# Revit family: Building-ConnessioniIEC309-GEWISS-67IB-PRESE-INTERBLOCCATE_IP67_SENZA_FONDO_FUS
name_source: partatom
category: Apparecchi elettrici
units: mm (PartAtom-declared; Revit-internal decimal feet)

## family parameters
Condiviso = Sì
Host = Superficie
Mantenere orientamento annotazione = Sì
Punto di calcolo locali = Sì
Quota connettore circolare = Usa diametro
Taglio con vuoti quando caricato = Sì
Tipo di parte = Normale

## types (23) — shared parameters
Catalogo = BUILDING
Catalogo Serie = 67 IB
Codice Electrocod = 2222
Con fondo = No
Corpo presa = GEWISS -BLU
Corrente nominale di cortocircuito (Icc) = 10KA
Frequenza = 50/60 Hz
Frequenza nominale (Hz) = 50/60 Hz
Glow Wire Test = 850 °C
Glow wire test: = 850 °C
Grado di protezione = IP67
IDF = 249aa0f0-cb6e-4699-9a5f-455441d8fc5e
IDT = 5410a18b-86cc-47a6-890a-93cf755ebe5d
Immagine tipo = G.jpg
Potere di interruzione fusibili = > 50 kA
Produttore = GEWISS S.p.A.
Prospetto di default = 1219 mm
Protezione = Base portafusibile (CBF)
Resistenza agli urti = IK08
SEO = Presa
Scheda Tecnica = https://www.gewiss.com
Simbolo presa = PRESAINDSTAGNA : 3P
Struttura = Grigio RAL - 7035
Temperatura di funzionamento = -25 ÷ +40 °C
Temperatura di utilizzo = -25 +40 °C
Tensione nominale di isolamento (Ui) = 500V
Tensione nominale di tenuta ad impulso = 4KV
Termopressione con biglia = 125 °C
Tipo fusibile = Ã˜ 10,3x38 mm
Tipologia = Verticale
URL = https://www.gewiss.com
Versione file RFA = 21.4
presa = rosso
zero-valued in all types: giallo

## per-type parameters (varying)
| type | Codice EAN | Colore | Colore: | Corrente nominale (A) | Corrente nominale (In) | Corrente nominale (In) presa IB | Descrizione | Modello | N. poli | Numero di poli | Peso | Peso (kg) | Riferimento h | Tensione nominale | Tensione nominale: |
| GW66323N - PR.BL IP67 S.F.2P+T 16A 110V 4H CBF | 8011564741782 | Giallo | Giallo | 16 | 16 | 16A | PR.BL IP67 S.F.2P+T 16A 110V 4H CBF | GW66323N | 2P+T | 2P+T | Max. 0,8 Kg | Max. 0,8 Kg | 4 | 100 - 130 V | 100 - 130 V |
| GW66332N - PR.BL IP67 S.F.3P+T 16A 500V 7H CBF | 8011564741874 | Nero | Nero | 16 | 16 | 16A | PR.BL IP67 S.F.3P+T 16A 500V 7H CBF | GW66332N | 3P+T | 3P+T | Max. 0,8 Kg | Max. 0,8 Kg | 7 | 480 - 500 V | 480 - 500 V |
| GW66344N - PR.BL IP67 S.F.3P+N+T 32A 500V 7H CBF | 8011564741997 | Nero | Nero | 32 | 32 | 28A | PR.BL IP67 S.F.3P+N+T 32A 500V 7H CBF | GW66344N | 3P+N+T | 3P+N+T | Max. 0,9 Kg | Max. 0,9 Kg | 7 | 480 - 500 V | 480 - 500 V |
| GW66324N - PR.BL IP67 S.F.3P+T 16A 110V 4H CBF | 8011564741799 | Giallo | Giallo | 16 | 16 | 16A | PR.BL IP67 S.F.3P+T 16A 110V 4H CBF | GW66324N | 3P+T | 3P+T | Max. 0,8 Kg | Max. 0,8 Kg | 4 | 100 - 130 V | 100 - 130 V |
| GW66338N - PR.BL IP67 S.F.3P+T 32A 230V 9H CBF | 8011564741935 | Blu | Blu | 32 | 32 | 28A | PR.BL IP67 S.F.3P+T 32A 230V 9H CBF | GW66338N | 3P+T | 3P+T | Max. 0,9 Kg | Max. 0,9 Kg | 9 | 200 - 250 V | 200 - 250 V |
| GW66326N - PR.BL IP67 S.F.2P+T 16A 230V 6H CBF | 8011564741812 | Blu | Blu | 16 | 16 | 16A | PR.BL IP67 S.F.2P+T 16A 230V 6H CBF | GW66326N | 2P+T | 2P+T | Max. 0,8 Kg | Max. 0,8 Kg | 6 | 200 - 250 V | 200 - 250 V |
| GW66339N - PR.BL IP67 S.F.3P+N+T 32A 230V 9H CBF | 8011564741942 | Blu | Blu | 32 | 32 | 28A | PR.BL IP67 S.F.3P+N+T 32A 230V 9H CBF | GW66339N | 3P+N+T | 3P+N+T | Max. 0,9 Kg | Max. 0,9 Kg | 9 | 200 - 250 V | 200 - 250 V |
| GW66325N - PR.BL IP67 S.F.3P+N+T 16A 110V 4H CBF | 8011564741805 | Giallo | Giallo | 16 | 16 | 16A | PR.BL IP67 S.F.3P+N+T 16A 110V 4H CBF | GW66325N | 3P+N+T | 3P+N+T | Max. 0,8 Kg | Max. 0,8 Kg | 4 | 100 - 130 V | 100 - 130 V |
| GW66333N - PR.BL IP67 S.F.3P+N+T 16A 500V 7H CBF | 8011564741881 | Nero | Nero | 16 | 16 | 16A | PR.BL IP67 S.F.3P+N+T 16A 500V 7H CBF | GW66333N | 3P+N+T | 3P+N+T | Max. 0,8 Kg | Max. 0,8 Kg | 7 | 480 - 500 V | 480 - 500 V |
| GW66337N - PR.BL IP67 S.F.2P+T 32A 230V 6H CBF | 8011564741928 | Blu | Blu | 32 | 32 | 32A | PR.BL IP67 S.F.2P+T 32A 230V 6H CBF | GW66337N | 2P+T | 2P+T | Max. 0,9 Kg | Max. 0,9 Kg | 6 | 200 - 250 V | 200 - 250 V |
| GW66358N - PR.BL IP67 S.F.3P+T 32A 380V 3H CBF | 8011564742123 | Rosso | Rosso | 32 | 32 | 28A | PR.BL IP67 S.F.3P+T 32A 380V 3H CBF | GW66358N | 3P+T | 3P+T | Max. 0,9 Kg | Max. 0,9 Kg | 3 | 380 - 440 V | 380 - 440 V |
| GW66329N - PR.BL IP67 S.F.2P+T 16A 400V 9H CBF | 8011564741843 | Rosso | Rosso | 16 | 16 | 16A | PR.BL IP67 S.F.2P+T 16A 400V 9H CBF | GW66329N | 2P+T | 2P+T | Max. 0,8 Kg | Max. 0,8 Kg | 9 | 380 - 415 V | 380 - 415 V |
| GW66330N - PR.BL IP67 S.F.3P+T 16A 400V 6H CBF | 8011564741850 | Rosso | Rosso | 16 | 16 | 16A | PR.BL IP67 S.F.3P+T 16A 400V 6H CBF | GW66330N | 3P+T | 3P+T | Max. 0,8 Kg | Max. 0,8 Kg | 6 | 380 - 415 V | 380 - 415 V |
| GW66342N - PR.BL IP67 S.F.3P+N+T 32A 400V 6H CBF | 8011564741973 | Rosso | Rosso | 32 | 32 | 28A | PR.BL IP67 S.F.3P+N+T 32A 400V 6H CBF | GW66342N | 3P+N+T | 3P+N+T | Max. 0,9 Kg | Max. 0,9 Kg | 6 | 380 - 415 V | 380 - 415 V |
| GW66327N - PR.BL IP67 S.F.3P+T 16A 230V 9H CBF | 8011564741829 | Blu | Blu | 16 | 16 | 16A | PR.BL IP67 S.F.3P+T 16A 230V 9H CBF | GW66327N | 3P+T | 3P+T | Max. 0,8 Kg | Max. 0,8 Kg | 9 | 200 - 250 V | 200 - 250 V |
| GW66331N - PR.BL IP67 S.F.3P+N+T 16A 400V 6H CBF | 8011564741867 | Rosso | Rosso | 16 | 16 | 16A | PR.BL IP67 S.F.3P+N+T 16A 400V 6H CBF | GW66331N | 3P+N+T | 3P+N+T | Max. 0,8 Kg | Max. 0,8 Kg | 6 | 380 - 415 V | 380 - 415 V |
| GW66343N - PR.BL IP67 S.F.3P+T 32A 500V 7H CBF | 8011564741980 | Nero | Nero | 32 | 32 | 28A | PR.BL IP67 S.F.3P+T 32A 500V 7H CBF | GW66343N | 3P+T | 3P+T | Max. 0,9 Kg | Max. 0,9 Kg | 7 | 480 - 500 V | 480 - 500 V |
| GW66336N - PR.BL IP67 S.F.3P+N+T 32A 110V 4H CBF | 8011564741911 | Giallo | Giallo | 32 | 32 | 28A | PR.BL IP67 S.F.3P+N+T 32A 110V 4H CBF | GW66336N | 3P+N+T | 3P+N+T | Max. 0,9 Kg | Max. 0,9 Kg | 4 | 100 - 130 V | 100 - 130 V |
| GW66328N - PR.BL IP67 S.F.3P+N+T 16A 230V 9H CBF | 8011564741836 | Blu | Blu | 16 | 16 | 16A | PR.BL IP67 S.F.3P+N+T 16A 230V 9H CBF | GW66328N | 3P+N+T | 3P+N+T | Max. 0,8 Kg | Max. 0,8 Kg | 9 | 200 - 250 V | 200 - 250 V |
| GW66335N - PR.BL IP67 S.F.3P+T 32A 110V 4H CBF | 8011564741904 | Giallo | Giallo | 32 | 32 | 28A | PR.BL IP67 S.F.3P+T 32A 110V 4H CBF | GW66335N | 3P+T | 3P+T | Max. 0,9 Kg | Max. 0,9 Kg | 4 | 100 - 130 V | 100 - 130 V |
| GW66334N - PR.BL IP67 S.F.2P+T 32A 110V 4H CBF | 8011564741898 | Giallo | Giallo | 32 | 32 | 32A | PR.BL IP67 S.F.2P+T 32A 110V 4H CBF | GW66334N | 2P+T | 2P+T | Max. 0,9 Kg | Max. 0,9 Kg | 4 | 100 - 130 V | 100 - 130 V |
| GW66340N - PR.BL IP67 S.F.2P+T 32A 400V 9H CBF | 8011564741959 | Rosso | Rosso | 32 | 32 | 32A | PR.BL IP67 S.F.2P+T 32A 400V 9H CBF | GW66340N | 2P+T | 2P+T | Max. 0,9 Kg | Max. 0,9 Kg | 9 | 380 - 415 V | 380 - 415 V |
| GW66341N - PR.BL IP67 S.F.3P+T 32A 400V 6H CBF | 8011564741966 | Rosso | Rosso | 32 | 32 | 28A | PR.BL IP67 S.F.3P+T 32A 400V 6H CBF | GW66341N | 3P+T | 3P+T | Max. 0,9 Kg | Max. 0,9 Kg | 6 | 380 - 415 V | 380 - 415 V |

## geometry (parser evidence)
native form markers: Sweep x4
no freeform markers — native parametric forms only
